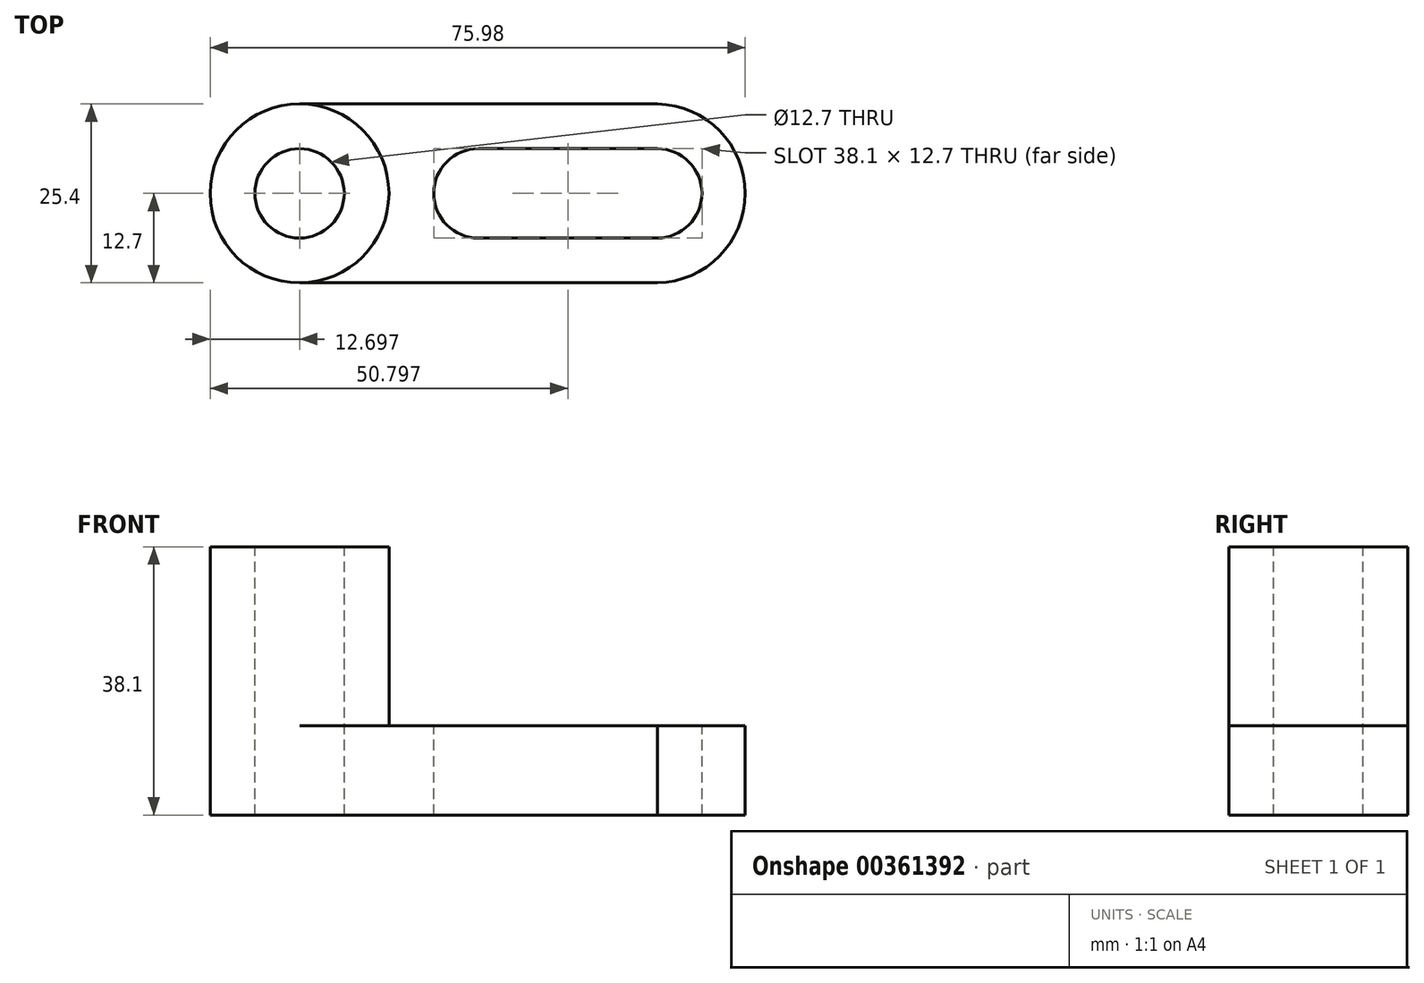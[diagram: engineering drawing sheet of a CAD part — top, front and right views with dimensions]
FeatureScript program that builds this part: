
annotation { "Feature Type Name" : "Feature", "Feature Type Description" : "" }
export const myFeature = defineFeature(function(context is Context, id is Id, definition is map)
    precondition{}
    {
        {
            var Q0;
            Q0=qCreatedBy(makeId("Front.planeOp"),FACE);
            var sketch = newSketch(context, id + "F0", { "sketchPlane" : qUnion([Q0])});
            skLineSegment(sketch, "E0", {"start": v(-32.22, 23.4) * mm, "end": v(-32.22, -14.7) * mm});
            skLineSegment(sketch, "E1", {"start": v(-32.22, -14.7) * mm, "end": v(43.98, -14.7) * mm});
            skLineSegment(sketch, "E2", {"start": v(43.98, -2) * mm, "end": v(43.98, -14.7) * mm});
            skLineSegment(sketch, "E3", {"start": v(43.98, -2) * mm, "end": v(-6.82, -2) * mm});
            skLineSegment(sketch, "E4", {"start": v(-6.82, 23.4) * mm, "end": v(-32.22, 23.4) * mm});
            skLineSegment(sketch, "E5", {"start": v(-6.82, 23.4) * mm, "end": v(-6.82, -2) * mm});
            skSolve(sketch);
        }
        {
            var Q0;
            Q0 = qSketchRegion(id + "F0", true);
            extrude(context, id + "F1", {"entities" : qUnion([Q0]), "depth" : 25.4 * mm});
        }
        {
            var Q0;
            Q0=makeQuery(id+"F1.opExtrude","SWEPT_FACE",FACE,{"disambiguationData":[OSD([sQuery(id+"F0.wireOp",EDGE,"E4")])]});
            var sketch = newSketch(context, id + "F2", { "sketchPlane" : qUnion([Q0])});
            skCircle(sketch, "E6", {"center": v(-19.52, -12.7) * mm, "radius": 12.7 * mm});
            skCircle(sketch, "E7", {"center": v(-19.52, -12.7) * mm, "radius": 6.35 * mm});
            skSolve(sketch);
        }
        {
            var Q0;
            {var subQ0=sQuery(id+"F2.wireOp",EDGE,"E6");var subQ1=sQuery(id+"F0.wireOp",EDGE,"E4");var subQ2=makeQuery(id+"F1.opExtrude","CAP_EDGE",EDGE,{"disambiguationData":[OSD([subQ1])],"isStart":true});var subQ3=makeQuery(id+"F2.imprint","INTERSECT",VERTEX,{"derivedFrom":[subQ2,subQ0]});Q0=makeQuery(id+"F2.imprint","IMPRINT",FACE,{"disambiguationData":[TD([[makeQuery(id+"F2.imprint","IMPRINT",EDGE,{"disambiguationData":[TD([[subQ3,-1.0]])],"derivedFrom":subQ0}),-1.0]])]});}
            var Q1;
            {var subQ0=sQuery(id+"F2.wireOp",EDGE,"E6");var subQ1=sQuery(id+"F0.wireOp",EDGE,"E4");var subQ4=makeQuery(id+"F1.opExtrude","CAP_EDGE",EDGE,{"disambiguationData":[OSD([subQ1])],"isStart":false});var subQ5=makeQuery(id+"F2.imprint","INTERSECT",VERTEX,{"derivedFrom":[subQ4,subQ0]});Q1=makeQuery(id+"F2.imprint","IMPRINT",FACE,{"disambiguationData":[TD([[makeQuery(id+"F2.imprint","IMPRINT",EDGE,{"disambiguationData":[TD([[subQ5,1.0]])],"derivedFrom":subQ0}),-1.0]])]});}
            var Q2;
            {var subQ0=sQuery(id+"F2.wireOp",EDGE,"E6");var subQ1=sQuery(id+"F0.wireOp",EDGE,"E4");var subQ4=makeQuery(id+"F1.opExtrude","CAP_EDGE",EDGE,{"disambiguationData":[OSD([subQ1])],"isStart":false});var subQ5=makeQuery(id+"F2.imprint","INTERSECT",VERTEX,{"derivedFrom":[subQ4,subQ0]});Q2=makeQuery(id+"F2.imprint","IMPRINT",FACE,{"disambiguationData":[TD([[makeQuery(id+"F2.imprint","IMPRINT",EDGE,{"disambiguationData":[TD([[subQ5,-1.0]])],"derivedFrom":subQ0}),-1.0]])]});}
            var Q3;
            {var subQ0=sQuery(id+"F2.wireOp",EDGE,"E6");var subQ1=sQuery(id+"F0.wireOp",EDGE,"E4");var subQ2=makeQuery(id+"F1.opExtrude","CAP_EDGE",EDGE,{"disambiguationData":[OSD([subQ1])],"isStart":true});var subQ3=makeQuery(id+"F2.imprint","INTERSECT",VERTEX,{"derivedFrom":[subQ2,subQ0]});Q3=makeQuery(id+"F2.imprint","IMPRINT",FACE,{"disambiguationData":[TD([[makeQuery(id+"F2.imprint","IMPRINT",EDGE,{"disambiguationData":[TD([[subQ3,1.0]])],"derivedFrom":subQ0}),-1.0]])]});}
            var Q4;
            Q4=makeQuery(id+"F2.imprint","IMPRINT",FACE,{"disambiguationData":[TD([[makeQuery(id+"F2.imprint","IMPRINT",EDGE,{"derivedFrom":sQuery(id+"F2.wireOp",EDGE,"E7")}),1.0]])]});
            extrude(context, id + "F3", {"entities" : qUnion([Q0, Q1, Q2, Q3, Q4]), "operationType" : NewBodyOperationType.REMOVE, "oppositeDirection" : true, "depth" : 25.4 * mm});
        }
        {
            var Q0;
            Q0=makeQuery(id+"F3.boolean.opBoolean","COPY",FACE,{"derivedFrom":makeQuery(id+"F3.opExtrude","CAP_FACE",FACE,{"disambiguationData":[OSD([sQuery(id+"F2.wireOp",EDGE,"E7")])],"isStart":false})});
            var Q1;
            {var subQ0=sQuery(id+"F0.wireOp",EDGE,"E4");var subQ1=makeQuery(id+"F1.opExtrude","CAP_EDGE",EDGE,{"disambiguationData":[OSD([subQ0])],"isStart":true});var subQ2=sQuery(id+"F0.wireOp",EDGE,"E0");var subQ3=makeQuery(id+"F1.opExtrude","SWEPT_EDGE",EDGE,{"disambiguationData":[OSD([subQ2,subQ0])]});var subQ4=makeQuery(id+"F2.imprint","INTERSECT",VERTEX,{"derivedFrom":[subQ3,subQ1]});var subQ5=sQuery(id+"F2.wireOp",EDGE,"E6");var subQ6=makeQuery(id+"F2.imprint","INTERSECT",VERTEX,{"derivedFrom":[subQ1,subQ5]});Q1=makeQuery(id+"F3.boolean.opBoolean","COPY",FACE,{"derivedFrom":makeQuery(id+"F3.opExtrude","CAP_FACE",FACE,{"disambiguationData":[OSD([subQ2,subQ0,subQ5]),TDD([makeQuery(id+"F2.imprint","IMPRINT",EDGE,{"disambiguationData":[TD([[subQ6,-1.0]])],"derivedFrom":subQ5}),makeQuery(id+"F2.imprint","IMPRINT",EDGE,{"disambiguationData":[TD([[subQ4,1.0]])],"derivedFrom":subQ3}),makeQuery(id+"F2.imprint","IMPRINT",EDGE,{"disambiguationData":[TD([[subQ6,-1.0]])],"derivedFrom":subQ1})])],"isStart":false})});}
            var Q2;
            {var subQ0=sQuery(id+"F0.wireOp",EDGE,"E4");var subQ1=makeQuery(id+"F1.opExtrude","CAP_EDGE",EDGE,{"disambiguationData":[OSD([subQ0])],"isStart":false});var subQ2=sQuery(id+"F0.wireOp",EDGE,"E0");var subQ3=makeQuery(id+"F1.opExtrude","SWEPT_EDGE",EDGE,{"disambiguationData":[OSD([subQ2,subQ0])]});var subQ4=makeQuery(id+"F2.imprint","INTERSECT",VERTEX,{"derivedFrom":[subQ3,subQ1]});var subQ5=sQuery(id+"F2.wireOp",EDGE,"E6");var subQ6=makeQuery(id+"F2.imprint","INTERSECT",VERTEX,{"derivedFrom":[subQ1,subQ5]});Q2=makeQuery(id+"F3.boolean.opBoolean","COPY",FACE,{"derivedFrom":makeQuery(id+"F3.opExtrude","CAP_FACE",FACE,{"disambiguationData":[OSD([subQ2,subQ0,subQ5]),TDD([makeQuery(id+"F2.imprint","IMPRINT",EDGE,{"disambiguationData":[TD([[subQ6,1.0]])],"derivedFrom":subQ5}),makeQuery(id+"F2.imprint","IMPRINT",EDGE,{"disambiguationData":[TD([[subQ4,-1.0]])],"derivedFrom":subQ3}),makeQuery(id+"F2.imprint","IMPRINT",EDGE,{"disambiguationData":[TD([[subQ6,-1.0]])],"derivedFrom":subQ1})])],"isStart":false})});}
            extrude(context, id + "F4", {"entities" : qUnion([Q0, Q1, Q2]), "operationType" : NewBodyOperationType.REMOVE, "oppositeDirection" : true, "depth" : 25.4 * mm});
        }
        {
            var Q0;
            {var subQ0=sQuery(id+"F0.wireOp",EDGE,"E4");var subQ1=makeQuery(id+"F1.opExtrude","CAP_EDGE",EDGE,{"disambiguationData":[OSD([subQ0])],"isStart":false});var subQ2=sQuery(id+"F0.wireOp",EDGE,"E5");var subQ3=makeQuery(id+"F1.opExtrude","SWEPT_EDGE",EDGE,{"disambiguationData":[OSD([subQ0,subQ2])]});var subQ4=makeQuery(id+"F2.imprint","INTERSECT",VERTEX,{"derivedFrom":[subQ3,subQ1]});var subQ5=sQuery(id+"F2.wireOp",EDGE,"E6");var subQ6=makeQuery(id+"F2.imprint","INTERSECT",VERTEX,{"derivedFrom":[subQ1,subQ5]});var subQ8=makeQuery(id+"F1.opExtrude","CAP_EDGE",EDGE,{"disambiguationData":[OSD([subQ0])],"isStart":true});var subQ9=makeQuery(id+"F2.imprint","INTERSECT",VERTEX,{"derivedFrom":[subQ3,subQ8]});var subQ10=makeQuery(id+"F2.imprint","INTERSECT",VERTEX,{"derivedFrom":[subQ8,subQ5]});Q0=makeQuery(id+"F3.boolean.opBoolean","MERGE",FACE,{"derivedFrom":[makeQuery(id+"F1.opExtrude","SWEPT_FACE",FACE,{"disambiguationData":[OSD([sQuery(id+"F0.wireOp",EDGE,"E3")])]}),makeQuery(id+"F3.opExtrude","CAP_FACE",FACE,{"disambiguationData":[OSD([subQ0,subQ2,subQ5]),TDD([makeQuery(id+"F2.imprint","IMPRINT",EDGE,{"disambiguationData":[TD([[subQ10,1.0]])],"derivedFrom":subQ5}),makeQuery(id+"F2.imprint","IMPRINT",EDGE,{"disambiguationData":[TD([[subQ9,1.0]])],"derivedFrom":subQ3}),makeQuery(id+"F2.imprint","IMPRINT",EDGE,{"disambiguationData":[TD([[subQ10,1.0]])],"derivedFrom":subQ8})])],"isStart":false}),makeQuery(id+"F3.opExtrude","CAP_FACE",FACE,{"disambiguationData":[OSD([subQ0,subQ2,subQ5]),TDD([makeQuery(id+"F2.imprint","IMPRINT",EDGE,{"disambiguationData":[TD([[subQ6,-1.0]])],"derivedFrom":subQ5}),makeQuery(id+"F2.imprint","IMPRINT",EDGE,{"disambiguationData":[TD([[subQ4,-1.0]])],"derivedFrom":subQ3}),makeQuery(id+"F2.imprint","IMPRINT",EDGE,{"disambiguationData":[TD([[subQ6,1.0]])],"derivedFrom":subQ1})])],"isStart":false})]});}
            var sketch = newSketch(context, id + "F5", { "sketchPlane" : qUnion([Q0])});
            skCircle(sketch, "E8", {"center": v(5.88, -12.7) * mm, "radius": 6.35 * mm});
            skCircle(sketch, "E9", {"center": v(31.28, -12.7) * mm, "radius": 6.35 * mm});
            skLineSegment(sketch, "E10.bottom", {"start": v(5.88, -6.35) * mm, "end": v(31.28, -6.35) * mm});
            skLineSegment(sketch, "E10.top", {"start": v(5.88, -19.05) * mm, "end": v(31.28, -19.05) * mm});
            skLineSegment(sketch, "E10.left", {"start": v(5.88, -6.35) * mm, "end": v(5.88, -19.05) * mm});
            skLineSegment(sketch, "E10.right", {"start": v(31.28, -6.35) * mm, "end": v(31.28, -19.05) * mm});
            skArc(sketch, "E11", {"start": v(31.28, -25.4) * mm, "mid": v(43.76, -12.7) * mm, "end": v(31.28, 0) * mm});
            skSolve(sketch);
        }
        {
            var Q0;
            Q0 = qSketchRegion(id + "F5", true);
            var Q1;
            {var subQ0=sQuery(id+"F5.wireOp",EDGE,"E11");Q1=makeQuery(id+"F5.imprint","IMPRINT",FACE,{"disambiguationData":[TD([[makeQuery(id+"F5.imprint","IMPRINT",EDGE,{"derivedFrom":subQ0}),-1.0]])]});}
            extrude(context, id + "F6", {"entities" : qUnion([Q0, Q1]), "operationType" : NewBodyOperationType.REMOVE, "oppositeDirection" : true, "depth" : 12.7 * mm});
        }
    });
